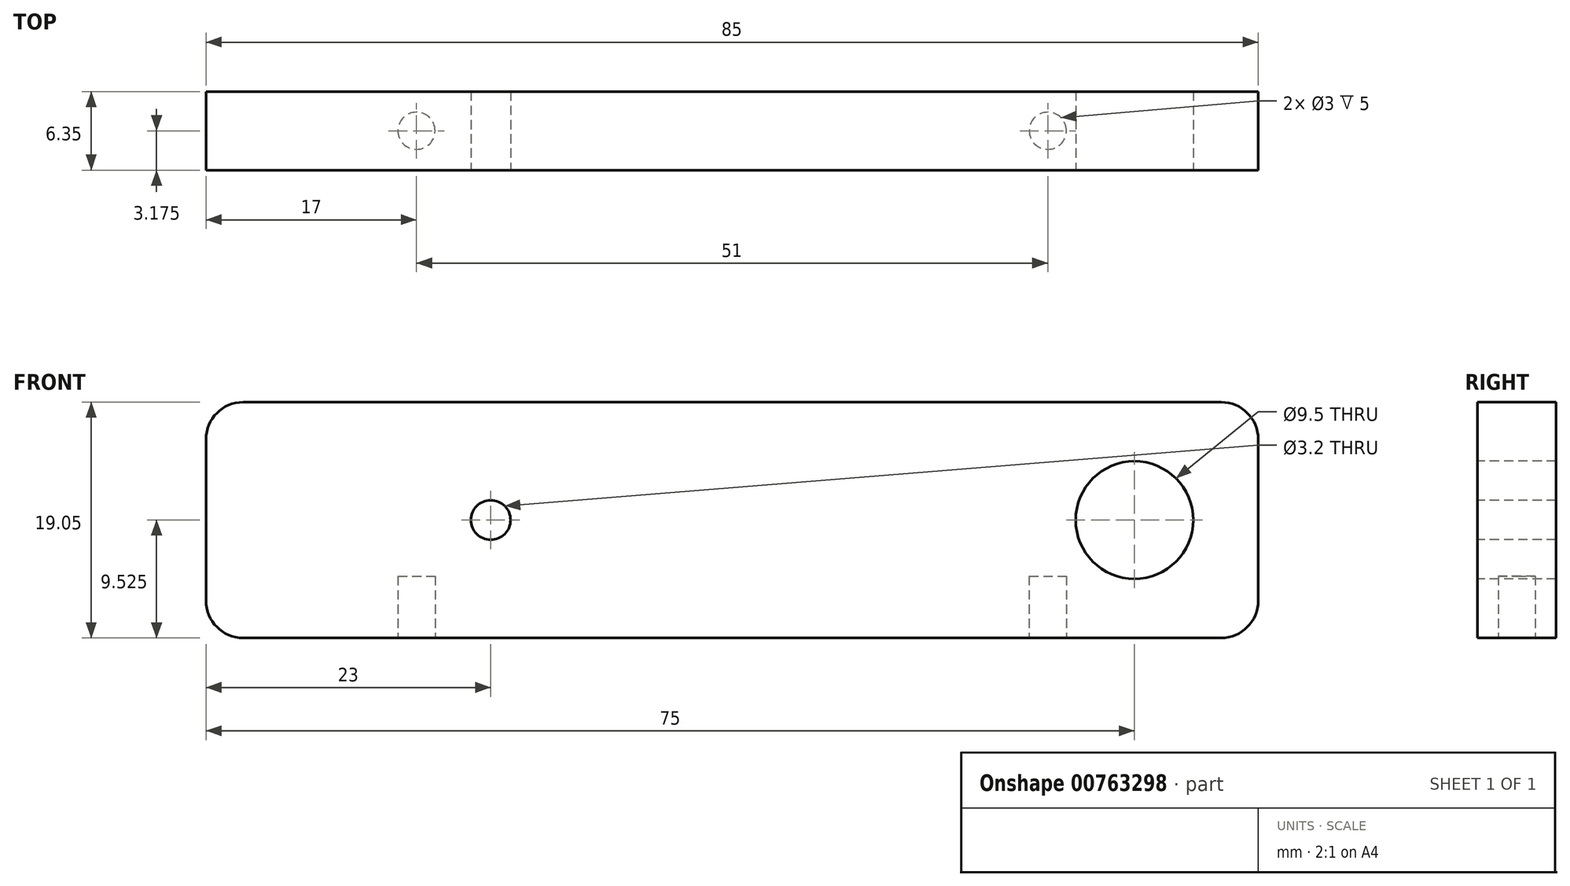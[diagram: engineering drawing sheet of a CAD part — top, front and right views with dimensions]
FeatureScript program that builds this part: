
annotation { "Feature Type Name" : "Feature", "Feature Type Description" : "" }
export const myFeature = defineFeature(function(context is Context, id is Id, definition is map)
    precondition{}
    {
        {
            var Q0;
            Q0=qCreatedBy(makeId("Front.planeOp"),FACE);
            var sketch = newSketch(context, id + "F0", { "sketchPlane" : qUnion([Q0])});
            skLineSegment(sketch, "E0.bottom", {"start": v(0, 0) * mm, "end": v(-85, 0) * mm});
            skLineSegment(sketch, "E0.top", {"start": v(0, 19.05) * mm, "end": v(-85, 19.05) * mm});
            skLineSegment(sketch, "E0.left", {"start": v(0, 0) * mm, "end": v(0, 19.05) * mm});
            skLineSegment(sketch, "E0.right", {"start": v(-85, 0) * mm, "end": v(-85, 19.05) * mm});
            skCircle(sketch, "E1", {"center": v(-10, 9.53) * mm, "radius": 4.75 * mm});
            skPoint(sketch, "E1.centerSnap0", {"position": v(0, 9.53) * mm});
            skCircle(sketch, "E2", {"center": v(-62, 9.53) * mm, "radius": 1.6 * mm});
            skSolve(sketch);
        }
        {
            var Q0;
            Q0=makeQuery(id+"F0.imprint","IMPRINT",FACE,{"disambiguationData":[TD([[makeQuery(id+"F0.imprint","IMPRINT",EDGE,{"derivedFrom":sQuery(id+"F0.wireOp",EDGE,"E0.bottom")}),-1.0]])]});
            extrude(context, id + "F1", {"entities" : qUnion([Q0]), "oppositeDirection" : true, "depth" : 6.35 * mm, "offsetDistance" : 25 * mm});
        }
        {
            var Q0;
            Q0=makeQuery(id+"F1.opExtrude","SWEPT_FACE",FACE,{"disambiguationData":[OSD([sQuery(id+"F0.wireOp",EDGE,"E0.bottom")])]});
            var sketch = newSketch(context, id + "F2", { "sketchPlane" : qUnion([Q0])});
            skCircle(sketch, "E3", {"center": v(-17, -3.17) * mm, "radius": 1.5 * mm});
            skPoint(sketch, "E3.centerSnap0", {"position": v(0, -3.17) * mm});
            skCircle(sketch, "E4", {"center": v(-68, -3.17) * mm, "radius": 1.5 * mm});
            skPoint(sketch, "E4.centerSnap0", {"position": v(-85, -3.17) * mm});
            skSolve(sketch);
        }
        {
            var Q0;
            Q0=makeQuery(id+"F2.imprint","IMPRINT",FACE,{"disambiguationData":[TD([[makeQuery(id+"F2.imprint","IMPRINT",EDGE,{"derivedFrom":sQuery(id+"F2.wireOp",EDGE,"E3")}),1.0]])]});
            var Q1;
            Q1=makeQuery(id+"F2.imprint","IMPRINT",FACE,{"disambiguationData":[TD([[makeQuery(id+"F2.imprint","IMPRINT",EDGE,{"derivedFrom":sQuery(id+"F2.wireOp",EDGE,"E4")}),1.0]])]});
            extrude(context, id + "F3", {"entities" : qUnion([Q0, Q1]), "operationType" : NewBodyOperationType.REMOVE, "oppositeDirection" : true, "depth" : 5 * mm, "offsetDistance" : 25 * mm});
        }
        {
            var Q0;
            Q0=makeQuery(id+"F1.opExtrude","SWEPT_EDGE",EDGE,{"disambiguationData":[OSD([sQuery(id+"F0.wireOp",EDGE,"E0.top"),sQuery(id+"F0.wireOp",EDGE,"E0.right")])]});
            var Q1;
            Q1=makeQuery(id+"F1.opExtrude","SWEPT_EDGE",EDGE,{"disambiguationData":[OSD([sQuery(id+"F0.wireOp",EDGE,"E0.bottom"),sQuery(id+"F0.wireOp",EDGE,"E0.right")])]});
            var Q2;
            Q2=makeQuery(id+"F1.opExtrude","SWEPT_EDGE",EDGE,{"disambiguationData":[OSD([sQuery(id+"F0.wireOp",EDGE,"E0.bottom"),sQuery(id+"F0.wireOp",EDGE,"E0.left")])]});
            var Q3;
            Q3=makeQuery(id+"F1.opExtrude","SWEPT_EDGE",EDGE,{"disambiguationData":[OSD([sQuery(id+"F0.wireOp",EDGE,"E0.top"),sQuery(id+"F0.wireOp",EDGE,"E0.left")])]});
            fillet(context, id + "F4", {"entities" : qUnion([Q0, Q1, Q2, Q3]), "radius" : 3 * mm, "tangentPropagation" : true, "allowEdgeOverflow" : false});
        }
    });
